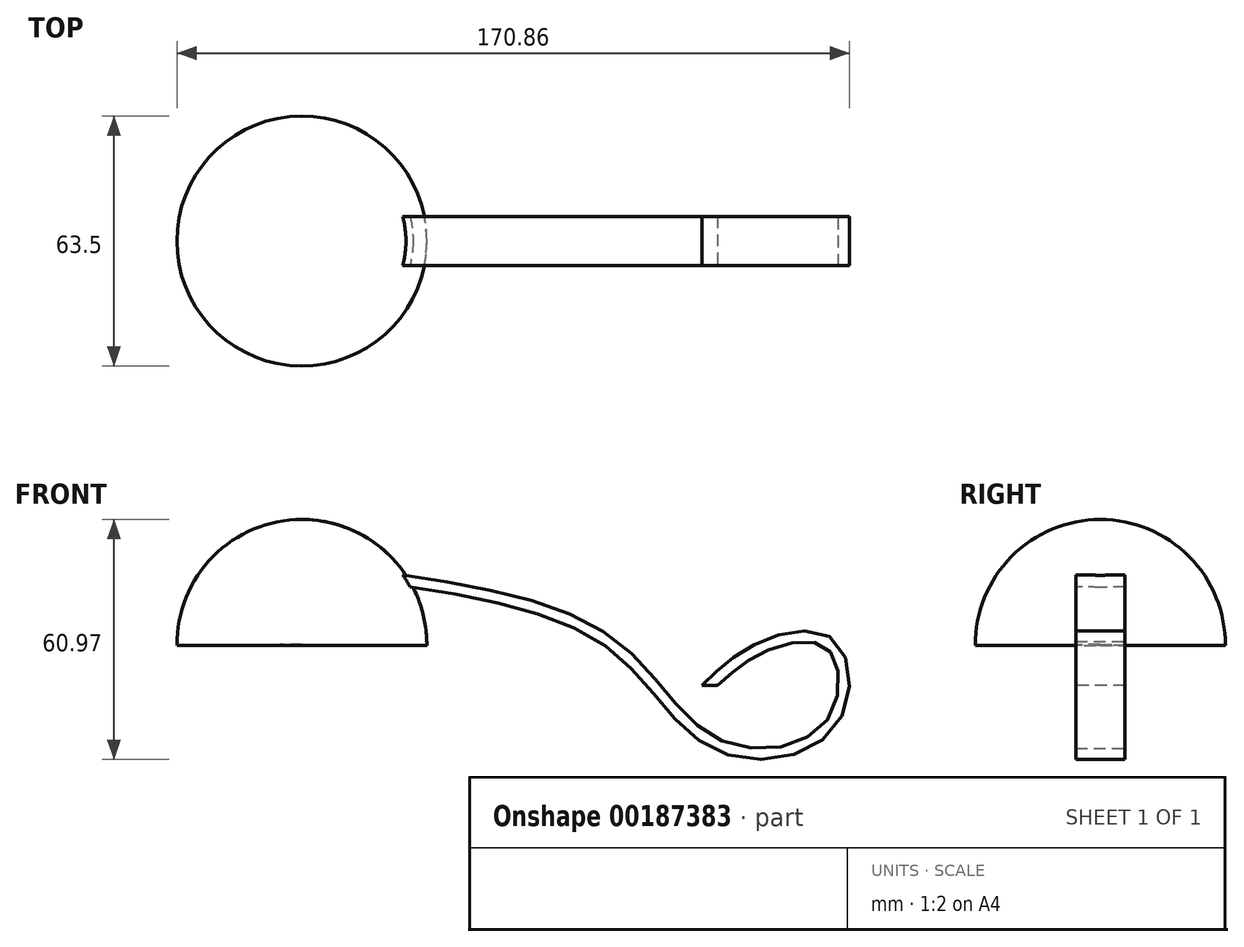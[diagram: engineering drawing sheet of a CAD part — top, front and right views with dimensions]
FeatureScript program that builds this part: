
annotation { "Feature Type Name" : "Feature", "Feature Type Description" : "" }
export const myFeature = defineFeature(function(context is Context, id is Id, definition is map)
    precondition{}
    {
        {
            var Q0;
            Q0=qCreatedBy(makeId("Front.planeOp"),FACE);
            var sketch = newSketch(context, id + "F0", { "sketchPlane" : qUnion([Q0])});
            skFitSpline(sketch, "E0", {"points": [v(-45.74, 27.3) * mm, v(10.58, 10.41) * mm, v(37.2, -15.02) * mm, v(65.36, -10.07) * mm, v(65.54, 10.24) * mm, v(47.62, 9.22) * mm, v(35.33, 0) * mm], "startDerivative": vector(266.6, -41.05) * mm, "endDerivative": vector(-84.47, -80.72) * mm});
            skSolve(sketch);
        }
        {
            var Q0;
            Q0=qCreatedBy(makeId("Top.planeOp"),FACE);
            var sketch = newSketch(context, id + "F1", { "sketchPlane" : qUnion([Q0])});
            skLineSegment(sketch, "E1.bottom", {"start": v(37.09, 6.27) * mm, "end": v(33.12, 6.27) * mm});
            skLineSegment(sketch, "E1.top", {"start": v(37.09, -6.27) * mm, "end": v(33.12, -6.27) * mm});
            skLineSegment(sketch, "E1.left", {"start": v(37.09, 6.27) * mm, "end": v(37.09, -6.27) * mm});
            skLineSegment(sketch, "E1.right", {"start": v(33.12, 6.27) * mm, "end": v(33.12, -6.27) * mm});
            skPoint(sketch, "E1.middle", {"position": v(35.1, 0) * mm});
            skSolve(sketch);
        }
        {
            var Q0;
            Q0=makeQuery(id+"F1.imprint","IMPRINT",FACE,{"disambiguationData":[TD([[makeQuery(id+"F1.imprint","IMPRINT",EDGE,{"derivedFrom":sQuery(id+"F1.wireOp",EDGE,"E1.bottom")}),1.0]])]});
            var Q1;
            Q1=sQuery(id+"F0.wireOp",EDGE,"E0");
            sweep(context, id + "F2", {"profiles" : qUnion([Q0]), "path" : qUnion([Q1])});
        }
        {
            var Q0;
            Q0=qCreatedBy(makeId("Front.planeOp"),FACE);
            var sketch = newSketch(context, id + "F3", { "sketchPlane" : qUnion([Q0])});
            skLineSegment(sketch, "E2", {"start": v(0, 0) * mm, "end": v(-68.56, 0) * mm, "construction": true});
            skLineSegment(sketch, "E3", {"start": v(-68.56, 0) * mm, "end": v(-68.56, 66.68) * mm, "construction": true});
            skSolve(sketch);
        }
        {
            var Q0;
            Q0=qCreatedBy(makeId("Front.planeOp"),FACE);
            var sketch = newSketch(context, id + "F4", { "sketchPlane" : qUnion([Q0])});
            skArc(sketch, "E4", {"start": v(-36.81, 10.11) * mm, "mid": v(-46.01, 32.74) * mm, "end": v(-68.56, 42.14) * mm});
            skLineSegment(sketch, "E5", {"start": v(-68.56, 42.14) * mm, "end": v(-68.56, 10.4) * mm});
            skLineSegment(sketch, "E6", {"start": v(-68.56, 10.4) * mm, "end": v(-36.81, 10.11) * mm});
            skSolve(sketch);
        }
        {
            var Q0;
            Q0=makeQuery(id+"F4.imprint","IMPRINT",FACE,{"disambiguationData":[TD([[makeQuery(id+"F4.imprint","IMPRINT",EDGE,{"derivedFrom":sQuery(id+"F4.wireOp",EDGE,"E4")}),1.0]])]});
            var Q1;
            Q1=sQuery(id+"F3.wireOp",EDGE,"E3");
            revolve(context, id + "F5", {"operationType" : NewBodyOperationType.ADD, "entities" : qUnion([Q0]), "axis" : qUnion([Q1]), "revolveType" : RevolveType.FULL});
        }
    });
